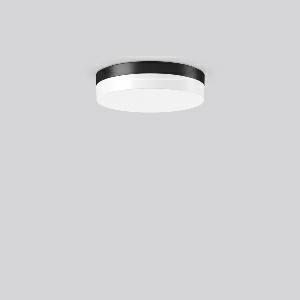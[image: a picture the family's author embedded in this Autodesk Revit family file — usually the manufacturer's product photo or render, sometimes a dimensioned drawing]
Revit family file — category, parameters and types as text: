
# Revit family: flat_slim_round_312630_0031_730_80d7
name_source: partatom
category: Lighting Fixtures
units: mm (PartAtom-declared; Revit-internal decimal feet)

## family parameters
Cut with Voids When Loaded = No
Host = Face
Light Source = No
Part Type = Normal
Room Calculation Point = No
Round Connector Dimension = Use Diameter
Shared = No

## types (1)
- MultiLumen 1 830 (1 x LED Modul 830, 1300 lm, 3000)
    Apparent Load = 11 VA
    CIE Flux Codes = 39 70 89 83 100
    Color Rendering = 80
    Color Temperature = 3000
    Default Elevation = 1800 mm
    Height = 70 mm
    Lamp = 1 x LED Modul 830
    Lamp Light Flux = 1300 lm
    Lamp count = 1
    Length = 300 mm
    Lifetime = 50000 h
    Luminous efficacy = 118 lm/W
    Manufacturer = RZB
    ModVariant = No
    Model = 312630.0031.730
    Mounting Place = Ceiling
    Mounting Type = Surface mounted
    Number of Poles = 1
    OnlyDefault = Yes
    Power Factor = 1
    Product Name = FLAT SLIM round
    Product group = Surface mounted ceiling and wall luminaires
    ProductGroupID = 305
    Protection Class = Protection class I
    Protection Degree = Degree of protection
    RLX_Detail_Level = 1
    RLX_Emergency_Light_Flux = 0 lm
    RLX_Emergency_Type = 0
    RLX_Emergency_Type_DB = No
    RlxData = <blob elided: 17525 chars, md5=7954eb95>
    Socket = socket
    Standby Power = 0 W
    System Light Flux = 1300 lm
    System Power = 11 W
    Type Comments = MultiLumen 1 830
    Type Image = 312629.0031.jpg
    URL = http://relux.com
    VarID = multilumen_1_830
    Voltage = 0 V
    Weight = 0.00 kg
    Width = 0 mm  [stored 0 ft]

note: [stored X ft] marks values corroborated as IEEE doubles in the binary element streams (Revit-internal decimal feet)

## geometry (parser evidence)
native form markers: Blend x4, Sweep x11
no freeform markers — native parametric forms only
